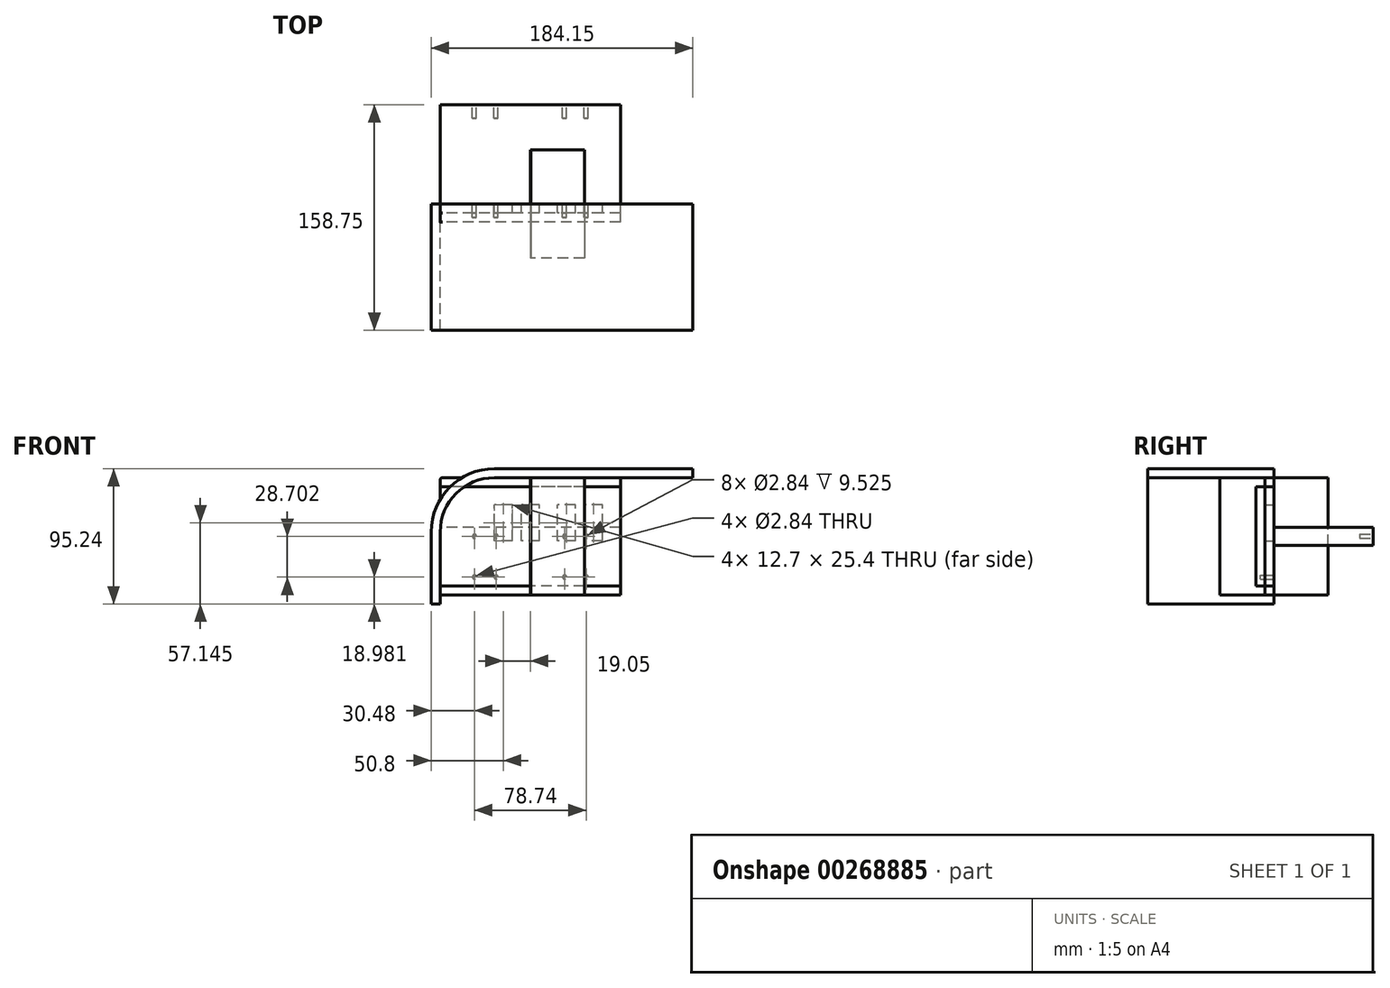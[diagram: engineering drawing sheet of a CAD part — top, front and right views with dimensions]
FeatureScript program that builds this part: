
annotation { "Feature Type Name" : "Feature", "Feature Type Description" : "" }
export const myFeature = defineFeature(function(context is Context, id is Id, definition is map)
    precondition{}
    {
        {
            assignVariable(context, id + "F0", {"name" : "plywoodthick", "anyValue" : .25});
        }
        {
            assignVariable(context, id + "F1", {"name" : "fillet", "anyValue" : 1.5});
        }
        {
            var Q0;
            Q0=qCreatedBy(makeId("Front.planeOp"),FACE);
            var sketch = newSketch(context, id + "F2", { "sketchPlane" : qUnion([Q0])});
            skLineSegment(sketch, "E0.bottom", {"start": v(63.5, -41.28) * mm, "end": v(-63.5, -41.28) * mm});
            skLineSegment(sketch, "E0.top", {"start": v(63.5, 41.28) * mm, "end": v(-63.5, 41.28) * mm});
            skLineSegment(sketch, "E0.left", {"start": v(63.5, -41.28) * mm, "end": v(63.5, 41.28) * mm});
            skLineSegment(sketch, "E0.right", {"start": v(-63.5, -41.28) * mm, "end": v(-63.5, 41.28) * mm});
            skPoint(sketch, "E0.middle", {"position": v(0, 0) * mm});
            skSolve(sketch);
        }
        {
            var Q0;
            Q0 = qSketchRegion(id + "F2", true);
            extrude(context, id + "F3", {"entities" : qUnion([Q0]), "depth" : 6.35 * mm});
        }
        {
            var Q0;
            Q0=qCreatedBy(makeId("Front.planeOp"),FACE);
            var sketch = newSketch(context, id + "F4", { "sketchPlane" : qUnion([Q0])});
            skLineSegment(sketch, "E1.0", {"start": v(63.5, -41.28) * mm, "end": v(63.5, 41.28) * mm, "construction": true});
            skLineSegment(sketch, "E2.0", {"start": v(63.5, 41.28) * mm, "end": v(-63.5, 41.28) * mm, "construction": true});
            skLineSegment(sketch, "E3.0", {"start": v(63.5, -41.28) * mm, "end": v(-63.5, -41.28) * mm, "construction": true});
            skLineSegment(sketch, "E4.0", {"start": v(-63.5, -41.28) * mm, "end": v(-63.5, 41.28) * mm, "construction": true});
            skLineSegment(sketch, "E5.bottom", {"start": v(50.8, -3.17) * mm, "end": v(38.1, -3.17) * mm});
            skLineSegment(sketch, "E5.top", {"start": v(50.8, 22.23) * mm, "end": v(38.1, 22.23) * mm});
            skLineSegment(sketch, "E5.left", {"start": v(50.8, -3.17) * mm, "end": v(50.8, 22.23) * mm});
            skLineSegment(sketch, "E5.right", {"start": v(38.1, -3.17) * mm, "end": v(38.1, 22.23) * mm});
            skPoint(sketch, "E5.middle", {"position": v(44.45, 9.53) * mm});
            skLineSegment(sketch, "E6", {"start": v(44.45, 9.53) * mm, "end": v(-44.45, 9.53) * mm, "construction": true});
            skLineSegment(sketch, "E7.bottom", {"start": v(31.75, -3.17) * mm, "end": v(19.05, -3.17) * mm});
            skLineSegment(sketch, "E7.top", {"start": v(31.75, 22.23) * mm, "end": v(19.05, 22.23) * mm});
            skLineSegment(sketch, "E7.left", {"start": v(31.75, -3.17) * mm, "end": v(31.75, 22.23) * mm});
            skLineSegment(sketch, "E7.right", {"start": v(19.05, -3.17) * mm, "end": v(19.05, 22.23) * mm});
            skPoint(sketch, "E7.middle", {"position": v(25.4, 9.53) * mm});
            skLineSegment(sketch, "E8.bottom", {"start": v(6.35, -3.17) * mm, "end": v(-6.35, -3.17) * mm});
            skLineSegment(sketch, "E8.top", {"start": v(6.35, 22.23) * mm, "end": v(-6.35, 22.23) * mm});
            skLineSegment(sketch, "E8.left", {"start": v(6.35, -3.17) * mm, "end": v(6.35, 22.23) * mm});
            skLineSegment(sketch, "E8.right", {"start": v(-6.35, -3.17) * mm, "end": v(-6.35, 22.23) * mm});
            skPoint(sketch, "E8.middle", {"position": v(0, 9.53) * mm});
            skLineSegment(sketch, "E9.bottom", {"start": v(-12.7, -3.17) * mm, "end": v(-25.4, -3.18) * mm});
            skLineSegment(sketch, "E9.top", {"start": v(-12.7, 22.23) * mm, "end": v(-25.4, 22.23) * mm});
            skLineSegment(sketch, "E9.left", {"start": v(-12.7, -3.17) * mm, "end": v(-12.7, 22.23) * mm});
            skLineSegment(sketch, "E9.right", {"start": v(-25.4, -3.18) * mm, "end": v(-25.4, 22.23) * mm});
            skPoint(sketch, "E9.middle", {"position": v(-19.05, 9.53) * mm});
            skSolve(sketch);
        }
        {
            var Q0;
            Q0 = qSketchRegion(id + "F4", true);
            extrude(context, id + "F5", {"entities" : qUnion([Q0]), "operationType" : NewBodyOperationType.REMOVE, "endBound" : BoundingType.UP_TO_NEXT, "depth" : 25.4 * mm});
        }
        {
            var Q0;
            Q0=qCreatedBy(makeId("Front.planeOp"),FACE);
            var sketch = newSketch(context, id + "F6", { "sketchPlane" : qUnion([Q0])});
            skLineSegment(sketch, "E10.bottom", {"start": v(63.5, -6.35) * mm, "end": v(-63.5, -6.35) * mm});
            skLineSegment(sketch, "E10.top", {"start": v(63.5, 6.35) * mm, "end": v(-63.5, 6.35) * mm});
            skLineSegment(sketch, "E10.left", {"start": v(63.5, -6.35) * mm, "end": v(63.5, 6.35) * mm});
            skLineSegment(sketch, "E10.right", {"start": v(-63.5, -6.35) * mm, "end": v(-63.5, 6.35) * mm});
            skPoint(sketch, "E10.middle", {"position": v(0, 0) * mm});
            skSolve(sketch);
        }
        {
            var Q0;
            Q0 = qSketchRegion(id + "F6", true);
            extrude(context, id + "F7", {"entities" : qUnion([Q0]), "oppositeDirection" : true, "depth" : 69.85 * mm});
        }
        {
            var Q0;
            Q0=makeQuery(id+"F7.opExtrude","CAP_FACE",FACE,{"disambiguationData":[OSD([sQuery(id+"F6.wireOp",EDGE,"E10.bottom"),sQuery(id+"F6.wireOp",EDGE,"E10.top"),sQuery(id+"F6.wireOp",EDGE,"E10.left"),sQuery(id+"F6.wireOp",EDGE,"E10.right")])],"isStart":false});
            var sketch = newSketch(context, id + "F8", { "sketchPlane" : qUnion([Q0])});
            skLineSegment(sketch, "E11.0", {"start": v(-63.5, 6.35) * mm, "end": v(63.5, 6.35) * mm, "construction": true});
            skLineSegment(sketch, "E12", {"start": v(-31.75, 6.35) * mm, "end": v(-31.75, 0.06) * mm, "construction": true});
            skLineSegment(sketch, "E13", {"start": v(-31.75, 0.06) * mm, "end": v(-39.37, 0.06) * mm, "construction": true});
            skCircle(sketch, "E14", {"center": v(-39.37, 0.06) * mm, "radius": 1.42 * mm});
            skCircle(sketch, "E15.MirrorC", {"center": v(-24.13, 0.06) * mm, "radius": 1.42 * mm});
            skCircle(sketch, "E16.MirrorC", {"center": v(24.13, 0.06) * mm, "radius": 1.42 * mm});
            skCircle(sketch, "E17.MirrorC", {"center": v(39.37, 0.06) * mm, "radius": 1.42 * mm});
            skSolve(sketch);
        }
        {
            var Q0;
            Q0 = qSketchRegion(id + "F8", true);
            extrude(context, id + "F9", {"entities" : qUnion([Q0]), "operationType" : NewBodyOperationType.REMOVE, "oppositeDirection" : true, "depth" : 9.52 * mm});
        }
        {
            var Q0;
            Q0=qCreatedBy(makeId("Right.planeOp"),FACE);
            var sketch = newSketch(context, id + "F10", { "sketchPlane" : qUnion([Q0])});
            skLineSegment(sketch, "E18.bottom", {"start": v(38.1, -41.27) * mm, "end": v(-38.1, -41.28) * mm});
            skLineSegment(sketch, "E18.top", {"start": v(38.1, 41.28) * mm, "end": v(-38.1, 41.27) * mm});
            skLineSegment(sketch, "E18.left", {"start": v(38.1, -41.27) * mm, "end": v(38.1, 41.28) * mm});
            skLineSegment(sketch, "E18.right", {"start": v(-38.1, -41.28) * mm, "end": v(-38.1, 41.27) * mm});
            skPoint(sketch, "E18.middle", {"position": v(0, 0) * mm});
            skSolve(sketch);
        }
        {
            var Q0;
            Q0 = qSketchRegion(id + "F10", true);
            extrude(context, id + "F11", {"entities" : qUnion([Q0]), "depth" : (getVariable(context, 'plywoodthick')) * mm});
        }
        {
            var Q0;
            Q0=qCreatedBy(makeId("Front.planeOp"),FACE);
            var sketch = newSketch(context, id + "F12", { "sketchPlane" : qUnion([Q0])});
            skLineSegment(sketch, "E19.bottom", {"start": v(63.5, -34.92) * mm, "end": v(-63.5, -34.93) * mm});
            skLineSegment(sketch, "E19.top", {"start": v(63.5, 34.93) * mm, "end": v(-63.5, 34.92) * mm});
            skLineSegment(sketch, "E19.left", {"start": v(63.5, -34.92) * mm, "end": v(63.5, 34.93) * mm});
            skLineSegment(sketch, "E19.right", {"start": v(-63.5, -34.93) * mm, "end": v(-63.5, 34.92) * mm});
            skPoint(sketch, "E19.middle", {"position": v(0, 0) * mm});
            skSolve(sketch);
        }
        {
            var Q0;
            Q0 = qSketchRegion(id + "F12", true);
            extrude(context, id + "F13", {"entities" : qUnion([Q0]), "depth" : 12.7 * mm});
        }
        {
            var Q0;
            Q0=makeQuery(id+"F13.opExtrude","SWEPT_EDGE",EDGE,{"disambiguationData":[OSD([sQuery(id+"F12.wireOp",EDGE,"E19.top"),sQuery(id+"F12.wireOp",EDGE,"E19.right")])]});
            var Q1;
            Q1=makeQuery(id+"F3.opExtrude","SWEPT_EDGE",EDGE,{"disambiguationData":[OSD([sQuery(id+"F2.wireOp",EDGE,"E0.top"),sQuery(id+"F2.wireOp",EDGE,"E0.right")])]});
            fillet(context, id + "F14", {"entities" : qUnion([Q0, Q1]), "radius" : (getVariable(context, 'fillet')) * mm, "tangentPropagation" : true, "allowEdgeOverflow" : false});
        }
        {
            var Q0;
            Q0=qCreatedBy(makeId("Front.planeOp"),FACE);
            var sketch = newSketch(context, id + "F15", { "sketchPlane" : qUnion([Q0])});
            skLineSegment(sketch, "E20.0", {"start": v(63.5, -34.92) * mm, "end": v(-63.5, -34.93) * mm, "construction": true});
            skLineSegment(sketch, "E21", {"start": v(0, -34.93) * mm, "end": v(0, -28.64) * mm, "construction": true});
            skLineSegment(sketch, "E22", {"start": v(7.62, -28.64) * mm, "end": v(-7.62, -28.64) * mm, "construction": true});
            skLineSegment(sketch, "E23", {"start": v(-31.75, -34.93) * mm, "end": v(-31.75, -28.64) * mm, "construction": true});
            skLineSegment(sketch, "E24", {"start": v(-24.13, -28.64) * mm, "end": v(-39.37, -28.64) * mm, "construction": true});
            skCircle(sketch, "E25", {"center": v(-39.37, -28.64) * mm, "radius": 1.42 * mm});
            skCircle(sketch, "E26", {"center": v(-24.13, -28.64) * mm, "radius": 1.42 * mm});
            skCircle(sketch, "E27.MirrorC", {"center": v(24.13, -28.64) * mm, "radius": 1.42 * mm});
            skCircle(sketch, "E28.MirrorC", {"center": v(39.37, -28.64) * mm, "radius": 1.42 * mm});
            skSolve(sketch);
        }
        {
            var Q0;
            Q0 = qSketchRegion(id + "F15", true);
            var Q1;
            Q1=makeQuery(id+"F13.opExtrude","CAP_FACE",FACE,{"disambiguationData":[OSD([sQuery(id+"F12.wireOp",EDGE,"E19.bottom"),sQuery(id+"F12.wireOp",EDGE,"E19.top"),sQuery(id+"F12.wireOp",EDGE,"E19.left"),sQuery(id+"F12.wireOp",EDGE,"E19.right")])],"isStart":false});
            extrude(context, id + "F16", {"entities" : qUnion([Q0]), "operationType" : NewBodyOperationType.REMOVE, "endBoundEntityFace" : qUnion([Q1]), "depth" : 9.52 * mm});
        }
        {
            var Q0;
            Q0=qCreatedBy(makeId("Front.planeOp"),FACE);
            var sketch = newSketch(context, id + "F17", { "sketchPlane" : qUnion([Q0])});
            skLineSegment(sketch, "E29.bottom", {"start": v(63.5, -41.28) * mm, "end": v(-63.5, -41.28) * mm, "construction": true});
            skLineSegment(sketch, "E29.top", {"start": v(63.5, 41.28) * mm, "end": v(-25.4, 41.28) * mm});
            skLineSegment(sketch, "E29.left", {"start": v(63.5, -41.28) * mm, "end": v(63.5, 41.27) * mm, "construction": true});
            skLineSegment(sketch, "E29.right", {"start": v(-63.5, -41.28) * mm, "end": v(-63.5, 3.18) * mm});
            skPoint(sketch, "E29.middle", {"position": v(0, 0) * mm});
            skLineSegment(sketch, "E30", {"start": v(-69.85, -41.28) * mm, "end": v(-69.85, 3.17) * mm});
            skLineSegment(sketch, "E31", {"start": v(-25.4, 47.62) * mm, "end": v(114.3, 47.62) * mm});
            skLineSegment(sketch, "E32", {"start": v(114.3, 47.63) * mm, "end": v(114.3, 41.27) * mm});
            skLineSegment(sketch, "E33", {"start": v(63.5, 41.28) * mm, "end": v(114.3, 41.28) * mm});
            skPoint(sketch, "E34.visualSharp", {"position": v(-63.5, 41.27) * mm});
            skArc(sketch, "E34.filletArc", {"start": v(-25.4, 41.28) * mm, "mid": v(-52.34, 30.12) * mm, "end": v(-63.5, 3.18) * mm});
            skPoint(sketch, "E35.visualSharp", {"position": v(-69.85, 47.62) * mm});
            skArc(sketch, "E35.filletArc", {"start": v(-25.4, 47.62) * mm, "mid": v(-56.83, 34.6) * mm, "end": v(-69.85, 3.17) * mm});
            skLineSegment(sketch, "E36", {"start": v(-69.85, -41.28) * mm, "end": v(-69.85, -47.63) * mm});
            skLineSegment(sketch, "E37", {"start": v(-69.85, -47.63) * mm, "end": v(-63.5, -47.63) * mm});
            skLineSegment(sketch, "E38", {"start": v(-63.5, -47.63) * mm, "end": v(-63.5, -41.28) * mm});
            skSolve(sketch);
        }
        {
            var Q0;
            Q0 = qSketchRegion(id + "F17", true);
            extrude(context, id + "F18", {"entities" : qUnion([Q0]), "depth" : 88.9 * mm});
        }
        {
            var Q0;
            Q0=qCreatedBy(makeId("Right.planeOp"),FACE);
            var sketch = newSketch(context, id + "F19", { "sketchPlane" : qUnion([Q0])});
            skLineSegment(sketch, "E39.bottom", {"start": v(38.1, -41.27) * mm, "end": v(-38.1, -41.28) * mm});
            skLineSegment(sketch, "E39.top", {"start": v(38.1, 41.28) * mm, "end": v(-38.1, 41.28) * mm});
            skLineSegment(sketch, "E39.left", {"start": v(38.1, -41.28) * mm, "end": v(38.1, 41.28) * mm});
            skLineSegment(sketch, "E39.right", {"start": v(-38.1, -41.28) * mm, "end": v(-38.1, 41.28) * mm});
            skPoint(sketch, "E39.middle", {"position": v(0, 0) * mm});
            skSolve(sketch);
        }
        {
            var Q0;
            Q0 = qSketchRegion(id + "F19", true);
            extrude(context, id + "F20", {"entities" : qUnion([Q0]), "depth" : 38.1 * mm});
        }
    });
